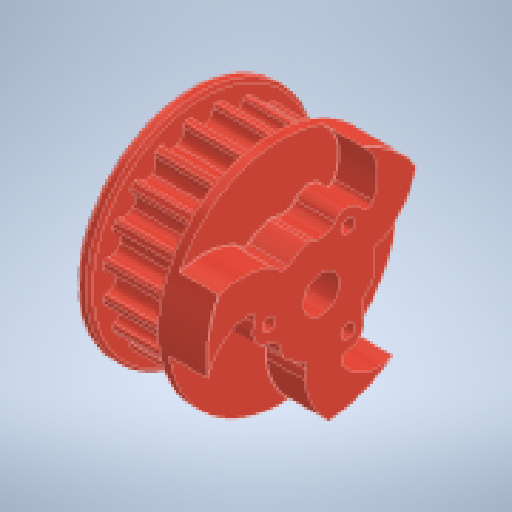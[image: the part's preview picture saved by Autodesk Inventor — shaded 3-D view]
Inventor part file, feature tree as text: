
AUTODESK INVENTOR PART (.ipt)
format: ipt  version: 2023.2 (Build 272271000, 271)  size: 1,039,360 bytes
history: native  units: in
note: dims shown in document units (in); Inventor stores cm internally (conversion verified against a paired STEP export)
features: extrude x4, sketch x4, other x4, thicken_offset x3, plane x2, fillet x2, chamfer x1, surface_op x1
ambient origin geometry x8: Origin, YZ Plane, XZ Plane, XY Plane, X Axis, Y Axis, Z Axis, Center Point
bodies: Solid1 (feature_tree), Body1 (feature_tree)
feature tree (21):
  extrude  "Extrusion1"  Depth=0.2165in
  plane  "Work Plane1"
  extrude  "Extrusion2"  [1 undecoded]
  chamfer  "Chamfer1"  Distance=0.3937in
  surface_op  "Sculpt1"
  extrude  "Extrusion3"  Depth=0.0039in
  sketch  "Sketch4"  dims[d8=0.0039in d9=0.0787in d10=45.0deg d11=0.2165in d12=1.1811in d14=360.0deg d16=0.0793in d17=0.0in d18=0.0in d19=1.378in d20=2.3622in d22=360.0deg d24=1.1811in d26=360.0deg d28=0.2362in d29=0.0in d32=0.0039in d33=0.0039in d34=0.0039in d35=0.0039in d36=0.0039in d37=0.0039in d38=0.0394in d39=0.0039in]
  plane  "Work Plane2"
  extrude  "Extrusion4"  Depth=0.0039in TaperAngle=360.0deg
  thicken_offset  "Thicken1"
  thicken_offset  "Thicken2"
  thicken_offset  "Thicken3"
  fillet  "Fillet3"  Radius=0.0793in
  fillet  "Fillet4"  [1 undecoded]
  sketch  "Sketch1"  dims[d0=0.4331in d1=0.2165in]
  sketch  "Sketch2"  dims[d2=0.3937in d3=0.0in d4=-0.0394in]
  sketch  "Sketch3"  dims[d5=1.3681in d6=0.3937in d7=0.0in]
  other  "Composite1"
  other  "Srf1"
  other  "Flash Hobby D3530 1100KV.iam"
  other  "Body - Basic:1"
note: 2 required parameter values undecoded (feature->parameter linkage not recoverable at this tier; creation-order binding heuristic only, values carry confidence <= 0.55)
